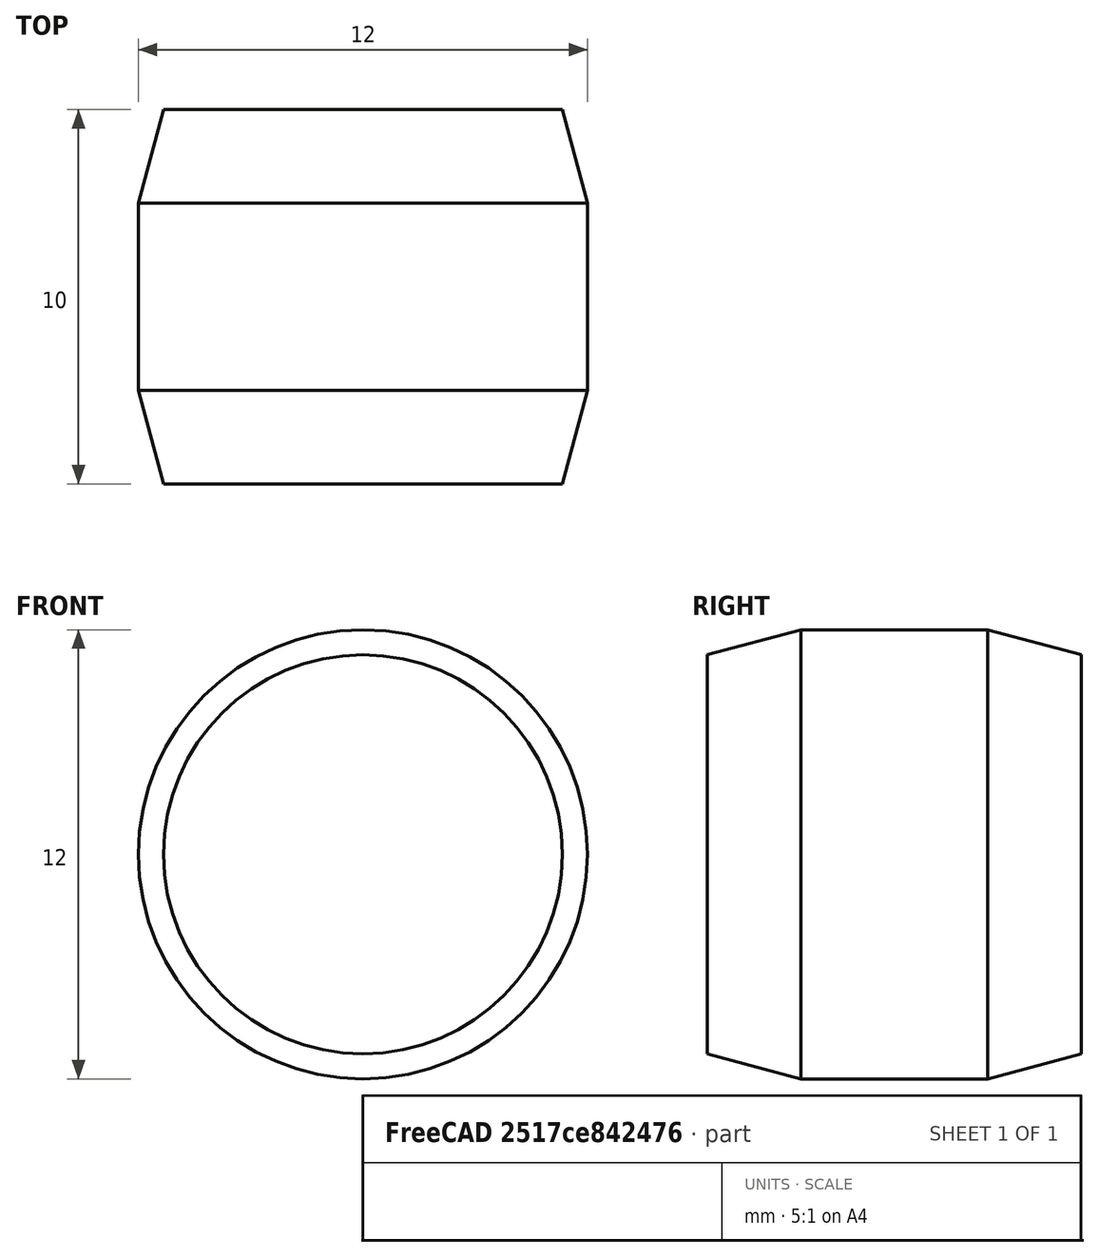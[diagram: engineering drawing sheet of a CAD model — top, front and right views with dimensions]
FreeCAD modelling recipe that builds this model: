
FCSTD DOCUMENT  (FreeCAD 0.15R4470 (Git))
Label: Zyl-Stift_ISO_8734-12x10
License: CC-BY 3.0
LicenseURL: http://creativecommons.org/licenses/by/3.0/
objects: Sketcher::SketchObject×1, PartDesign::Revolution×1
note: 3 computed .brp shape members not serialized (recipe doc carries the construction recipe); baked Part::Feature solids carry a one-line shape summary decoded from their .brp

FEATURE [Sketcher::SketchObject] Sketch
  Placement = pos=(0,0,0) rot=(0.57735,0.57735,0.57735;2.0944rad)
  sketch-geometry (7):
    g0: LineSegment StartX=0 StartY=0 StartZ=0 EndX=0 EndY=5.33013 EndZ=0
    g1: LineSegment StartX=0 StartY=5.33013 StartZ=0 EndX=2.5 EndY=6 EndZ=0
    g2: LineSegment StartX=2.5 StartY=6 StartZ=0 EndX=7.5 EndY=6 EndZ=0
    g3: LineSegment StartX=7.5 StartY=6 StartZ=0 EndX=10 EndY=5.33013 EndZ=0
    g4: LineSegment StartX=10 StartY=5.33013 StartZ=0 EndX=10 EndY=0 EndZ=0
    g5: LineSegment StartX=10 StartY=0 StartZ=0 EndX=0 EndY=0 EndZ=0
    g6: LineSegment [constr] StartX=0 StartY=5.33013 StartZ=0 EndX=10 EndY=5.33013 EndZ=0
  constraints (19):
    c: Coincident(g0,g-1)
    c: PointOnObject(g0,g-2)
    c: Coincident(g0,g1)
    c: Coincident(g1,g2)
    c: Horizontal(g2)
    c: Coincident(g2,g3)
    c: Coincident(g3,g4)
    c: Vertical(g4)
    c: Coincident(g4,g5)
    c: Coincident(g5,g-1)
    c: Horizontal(g5)
    c: Equal(g3,g1)
    c: Coincident(g6,g0)
    c: Coincident(g6,g3)
    c: Horizontal(g6)
    c: Angle(g6,g1) = 0.261799
    c: DistanceY(g-1,g1) = 6
    c: DistanceX(g5) = -10
    c: DistanceX(g1) = 2.5
FEATURE [PartDesign::Revolution] Revolution  label="Zyl-Stift ISO 8734-12x10 #"
  Angle = 360
  Axis = (0,1,0)
  Base = (0,0,0)
  Placement = pos=(0,0,0) rot=(0.57735,0.57735,0.57735;2.0944rad)
  ReferenceAxis = -> Sketch [H_Axis]
  Sketch = -> Sketch
